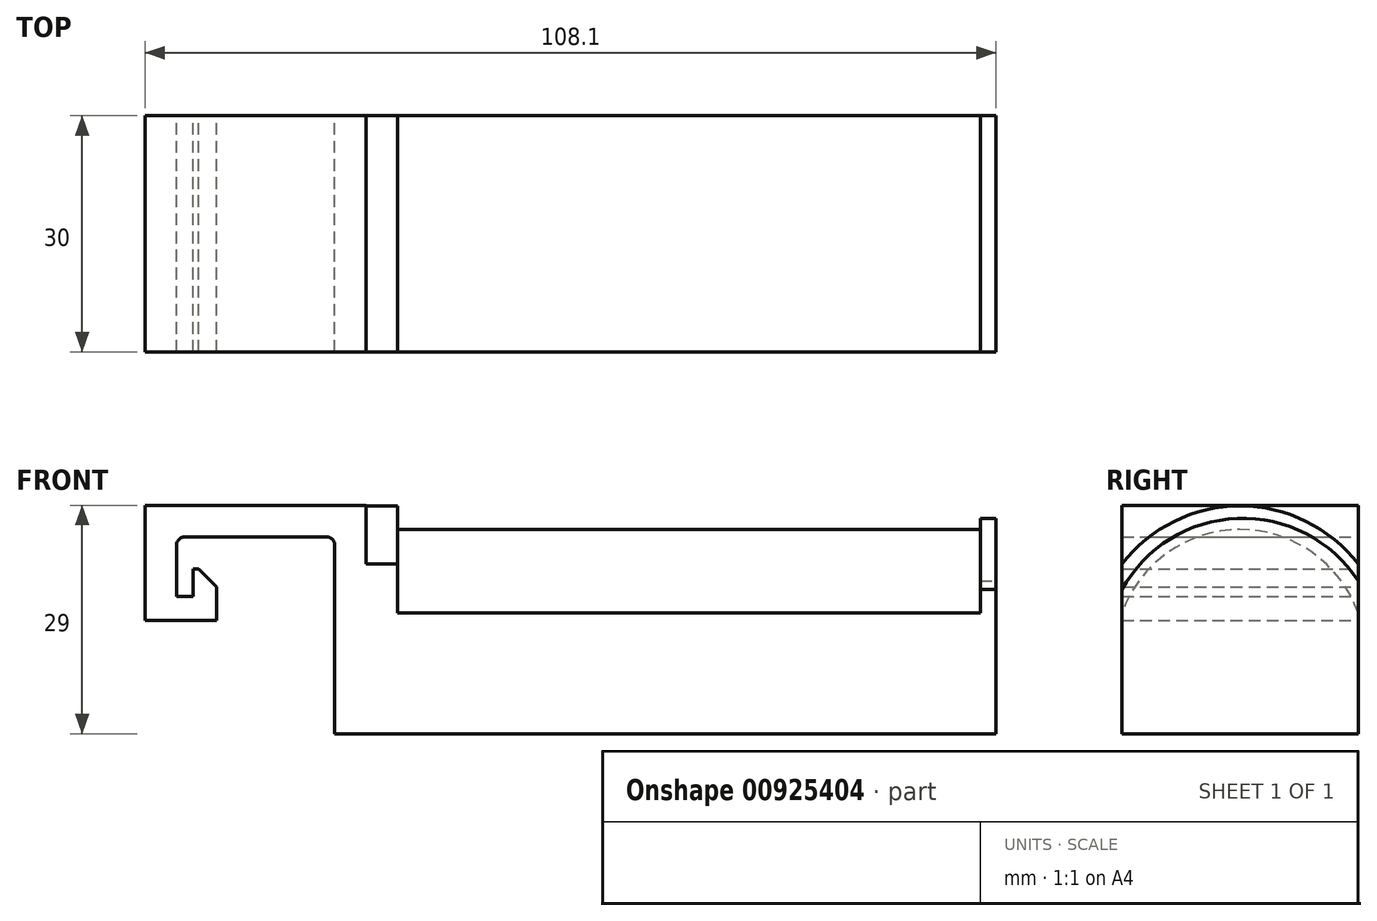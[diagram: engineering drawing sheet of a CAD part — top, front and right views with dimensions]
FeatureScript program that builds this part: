
annotation { "Feature Type Name" : "Feature", "Feature Type Description" : "" }
export const myFeature = defineFeature(function(context is Context, id is Id, definition is map)
    precondition{}
    {
        {
            var Q0;
            Q0=qCreatedBy(makeId("Front.planeOp"),FACE);
            var sketch = newSketch(context, id + "F0", { "sketchPlane" : qUnion([Q0])});
            skLineSegment(sketch, "E0", {"start": v(-34.86, 21.27) * mm, "end": v(-34.86, -2.73) * mm});
            skLineSegment(sketch, "E1", {"start": v(-22.86, 9.27) * mm, "end": v(-46.86, 9.27) * mm});
            skLineSegment(sketch, "E2", {"start": v(-25.86, 19.27) * mm, "end": v(-43.86, 19.27) * mm});
            skLineSegment(sketch, "E3", {"start": v(-25.86, -0.73) * mm, "end": v(-31.56, -0.73) * mm});
            skLineSegment(sketch, "E4", {"start": v(-24.86, 18.27) * mm, "end": v(-24.86, 0.27) * mm});
            skLineSegment(sketch, "E5", {"start": v(-44.86, 18.27) * mm, "end": v(-44.86, 12.57) * mm});
            skLineSegment(sketch, "E6", {"start": v(-30.86, 10.27) * mm, "end": v(-30.86, 6.54) * mm});
            skLineSegment(sketch, "E7", {"start": v(-38.86, 12.21) * mm, "end": v(-38.86, 9.93) * mm});
            skLineSegment(sketch, "E8", {"start": v(-33.86, 13.27) * mm, "end": v(-37.59, 13.27) * mm});
            skLineSegment(sketch, "E9", {"start": v(-27.86, 17.27) * mm, "end": v(-40.36, 17.27) * mm});
            skLineSegment(sketch, "E10", {"start": v(-26.86, 16.27) * mm, "end": v(-26.86, 3.77) * mm});
            skLineSegment(sketch, "E11", {"start": v(-42.86, 15.27) * mm, "end": v(-42.86, 12.57) * mm});
            skLineSegment(sketch, "E12", {"start": v(-43.16, 12.27) * mm, "end": v(-44.56, 12.27) * mm});
            skLineSegment(sketch, "E13", {"start": v(-43.16, 6.27) * mm, "end": v(-44.56, 6.27) * mm});
            skLineSegment(sketch, "E14", {"start": v(-41.92, 3.27) * mm, "end": v(-42.86, 3.27) * mm});
            skLineSegment(sketch, "E15", {"start": v(-42.86, 5.97) * mm, "end": v(-42.86, 3.27) * mm});
            skLineSegment(sketch, "E16", {"start": v(-44.86, 5.97) * mm, "end": v(-44.86, 0.27) * mm});
            skLineSegment(sketch, "E17", {"start": v(-41.92, 15.27) * mm, "end": v(-42.86, 15.27) * mm});
            skLineSegment(sketch, "E18", {"start": v(-38.79, 8.87) * mm, "end": v(-38.56, 9.27) * mm});
            skLineSegment(sketch, "E19", {"start": v(-38.79, 9.68) * mm, "end": v(-38.56, 9.27) * mm});
            skLineSegment(sketch, "E20", {"start": v(-38.86, 6.77) * mm, "end": v(-38.86, 6.33) * mm});
            skLineSegment(sketch, "E21", {"start": v(-38.86, 12.21) * mm, "end": v(-41.92, 15.27) * mm});
            skLineSegment(sketch, "E22", {"start": v(-38.86, 6.33) * mm, "end": v(-41.92, 3.27) * mm});
            skLineSegment(sketch, "E23", {"start": v(-38.86, 6.77) * mm, "end": v(-38.6, 8.05) * mm});
            skArc(sketch, "E24", {"start": v(-38.79, 8.87) * mm, "mid": v(-38.86, 8.62) * mm, "end": v(-38.79, 8.37) * mm});
            skLineSegment(sketch, "E25", {"start": v(-38.79, 8.37) * mm, "end": v(-38.6, 8.05) * mm});
            skArc(sketch, "E26", {"start": v(-38.86, 9.93) * mm, "mid": v(-38.84, 9.8) * mm, "end": v(-38.79, 9.68) * mm});
            skArc(sketch, "E27", {"start": v(-43.16, 12.27) * mm, "mid": v(-42.94, 12.36) * mm, "end": v(-42.86, 12.57) * mm});
            skArc(sketch, "E28", {"start": v(-44.86, 12.57) * mm, "mid": v(-44.77, 12.36) * mm, "end": v(-44.56, 12.27) * mm});
            skArc(sketch, "E29", {"start": v(-42.86, 5.97) * mm, "mid": v(-42.94, 6.19) * mm, "end": v(-43.16, 6.27) * mm});
            skArc(sketch, "E30", {"start": v(-44.56, 6.27) * mm, "mid": v(-44.77, 6.19) * mm, "end": v(-44.86, 5.97) * mm});
            skLineSegment(sketch, "E31", {"start": v(-37.8, 5.27) * mm, "end": v(-35.51, 5.27) * mm});
            skLineSegment(sketch, "E32", {"start": v(-32.36, 5.27) * mm, "end": v(-31.92, 5.27) * mm});
            skArc(sketch, "E33", {"start": v(-38.16, -0.73) * mm, "mid": v(-37.94, -0.64) * mm, "end": v(-37.86, -0.43) * mm});
            skLineSegment(sketch, "E34", {"start": v(-40.86, 1.27) * mm, "end": v(-38.16, 1.27) * mm});
            skArc(sketch, "E35", {"start": v(-37.86, 0.97) * mm, "mid": v(-37.94, 1.19) * mm, "end": v(-38.16, 1.27) * mm});
            skLineSegment(sketch, "E36", {"start": v(-31.56, 1.27) * mm, "end": v(-28.86, 1.27) * mm});
            skArc(sketch, "E37", {"start": v(-31.56, 1.27) * mm, "mid": v(-31.77, 1.19) * mm, "end": v(-31.86, 0.97) * mm});
            skLineSegment(sketch, "E38", {"start": v(-28.86, 2.21) * mm, "end": v(-28.86, 1.27) * mm});
            skLineSegment(sketch, "E39", {"start": v(-40.86, 2.21) * mm, "end": v(-40.86, 1.27) * mm});
            skLineSegment(sketch, "E40", {"start": v(-31.86, 0.97) * mm, "end": v(-31.86, -0.43) * mm});
            skArc(sketch, "E41", {"start": v(-31.86, -0.43) * mm, "mid": v(-31.77, -0.64) * mm, "end": v(-31.56, -0.73) * mm});
            skLineSegment(sketch, "E42", {"start": v(-37.86, 0.97) * mm, "end": v(-37.86, -0.43) * mm});
            skLineSegment(sketch, "E43", {"start": v(-34.45, 5.34) * mm, "end": v(-34.86, 5.57) * mm});
            skLineSegment(sketch, "E44", {"start": v(-35.26, 5.34) * mm, "end": v(-34.86, 5.57) * mm});
            skArc(sketch, "E45", {"start": v(-35.51, 5.27) * mm, "mid": v(-35.38, 5.3) * mm, "end": v(-35.26, 5.34) * mm});
            skLineSegment(sketch, "E46", {"start": v(-31.92, 5.27) * mm, "end": v(-28.86, 2.21) * mm});
            skLineSegment(sketch, "E47", {"start": v(-37.8, 5.27) * mm, "end": v(-40.86, 2.21) * mm});
            skLineSegment(sketch, "E48", {"start": v(-32.36, 5.27) * mm, "end": v(-33.64, 5.52) * mm});
            skArc(sketch, "E49", {"start": v(-34.45, 5.34) * mm, "mid": v(-34.2, 5.27) * mm, "end": v(-33.95, 5.34) * mm});
            skLineSegment(sketch, "E50", {"start": v(-33.95, 5.34) * mm, "end": v(-33.64, 5.52) * mm});
            skLineSegment(sketch, "E51", {"start": v(-38.16, -0.73) * mm, "end": v(-43.86, -0.73) * mm});
            skLineSegment(sketch, "E52", {"start": v(-30.7, 6.19) * mm, "end": v(-27.94, 3.42) * mm});
            skLineSegment(sketch, "E53", {"start": v(-37.94, 13.42) * mm, "end": v(-40.7, 16.19) * mm});
            skLineSegment(sketch, "E54", {"start": v(-40.86, 16.77) * mm, "end": v(-40.86, 16.54) * mm});
            skLineSegment(sketch, "E55", {"start": v(-27.36, 3.27) * mm, "end": v(-27.59, 3.27) * mm});
            skCircle(sketch, "E56", {"center": v(-34.86, 9.27) * mm, "radius": 2.1 * mm});
            skArc(sketch, "E57", {"start": v(-26.86, 16.27) * mm, "mid": v(-27.15, 16.98) * mm, "end": v(-27.86, 17.27) * mm});
            skArc(sketch, "E58", {"start": v(-24.86, 18.27) * mm, "mid": v(-25.15, 18.98) * mm, "end": v(-25.86, 19.27) * mm});
            skArc(sketch, "E59", {"start": v(-25.86, -0.73) * mm, "mid": v(-25.15, -0.43) * mm, "end": v(-24.86, 0.27) * mm});
            skArc(sketch, "E60", {"start": v(-44.86, 0.27) * mm, "mid": v(-44.56, -0.43) * mm, "end": v(-43.86, -0.73) * mm});
            skArc(sketch, "E61", {"start": v(-43.86, 19.27) * mm, "mid": v(-44.56, 18.98) * mm, "end": v(-44.86, 18.27) * mm});
            skArc(sketch, "E62", {"start": v(-27.36, 3.27) * mm, "mid": v(-27, 3.42) * mm, "end": v(-26.86, 3.77) * mm});
            skArc(sketch, "E63", {"start": v(-27.94, 3.42) * mm, "mid": v(-27.78, 3.31) * mm, "end": v(-27.59, 3.27) * mm});
            skArc(sketch, "E64", {"start": v(-40.36, 17.27) * mm, "mid": v(-40.7, 17.13) * mm, "end": v(-40.86, 16.77) * mm});
            skArc(sketch, "E65", {"start": v(-40.86, 16.54) * mm, "mid": v(-40.82, 16.35) * mm, "end": v(-40.7, 16.19) * mm});
            skArc(sketch, "E66", {"start": v(-37.94, 13.42) * mm, "mid": v(-37.78, 13.31) * mm, "end": v(-37.59, 13.27) * mm});
            skArc(sketch, "E67", {"start": v(-30.86, 6.54) * mm, "mid": v(-30.82, 6.35) * mm, "end": v(-30.7, 6.19) * mm});
            skArc(sketch, "E68", {"start": v(-30.86, 10.27) * mm, "mid": v(-31.74, 12.4) * mm, "end": v(-33.86, 13.27) * mm});
            skSolve(sketch);
        }
        {
            var Q0;
            Q0=makeQuery(id+"F0.imprint","IMPRINT",FACE,{"disambiguationData":[TD([[makeQuery(id+"F0.imprint","IMPRINT",EDGE,{"derivedFrom":sQuery(id+"F0.wireOp",EDGE,"E5")}),1.0]])]});
            var sketch = newSketch(context, id + "F1", { "sketchPlane" : qUnion([Q0])});
            skLineSegment(sketch, "E69.bottom", {"start": v(-42.14, 15.3) * mm, "end": v(-42.83, 15.3) * mm});
            skLineSegment(sketch, "E69.top", {"start": v(-39.83, 8.8) * mm, "end": v(-42.83, 8.8) * mm});
            skLineSegment(sketch, "E69.left", {"start": v(-39.83, 13.02) * mm, "end": v(-39.83, 8.8) * mm});
            skLineSegment(sketch, "E69.right", {"start": v(-42.83, 15.3) * mm, "end": v(-42.83, 8.8) * mm});
            skLineSegment(sketch, "E70.bottom", {"start": v(-42.83, 8.8) * mm, "end": v(-48.93, 8.8) * mm});
            skLineSegment(sketch, "E70.top", {"start": v(-42.83, 11.8) * mm, "end": v(-48.93, 11.8) * mm});
            skLineSegment(sketch, "E70.left", {"start": v(-42.83, 8.8) * mm, "end": v(-42.83, 11.8) * mm});
            skLineSegment(sketch, "E70.right", {"start": v(-48.93, 8.8) * mm, "end": v(-48.93, 11.8) * mm});
            skLineSegment(sketch, "E71.bottom", {"start": v(-48.93, 11.8) * mm, "end": v(-44.93, 11.8) * mm});
            skLineSegment(sketch, "E71.left", {"start": v(-48.93, 11.8) * mm, "end": v(-48.93, 23.39) * mm});
            skLineSegment(sketch, "E71.right", {"start": v(-44.93, 11.8) * mm, "end": v(-44.93, 18.33) * mm});
            skLineSegment(sketch, "E72.bottom", {"start": v(-48.93, 23.39) * mm, "end": v(-20.85, 23.39) * mm});
            skLineSegment(sketch, "E72.top", {"start": v(-43.87, 19.39) * mm, "end": v(-25.83, 19.39) * mm});
            skLineSegment(sketch, "E72.right", {"start": v(-20.85, 23.39) * mm, "end": v(-20.83, 19.39) * mm});
            skLineSegment(sketch, "E73.bottom", {"start": v(-20.83, 14.39) * mm, "end": v(-24.83, 14.39) * mm});
            skLineSegment(sketch, "E73.top", {"start": v(-20.83, -5.61) * mm, "end": v(-24.83, -5.61) * mm});
            skLineSegment(sketch, "E73.left", {"start": v(-20.83, 14.39) * mm, "end": v(-20.83, -5.61) * mm});
            skLineSegment(sketch, "E73.right", {"start": v(-24.83, 18.39) * mm, "end": v(-24.83, -5.61) * mm});
            skArc(sketch, "E74.filletArc", {"start": v(-43.87, 19.39) * mm, "mid": v(-44.62, 19.08) * mm, "end": v(-44.93, 18.33) * mm});
            skPoint(sketch, "E75.visualSharp", {"position": v(-39.83, 15.3) * mm});
            skPoint(sketch, "E76", {"position": v(-65.12, 18.75) * mm});
            skLineSegment(sketch, "E77", {"start": v(-42.14, 15.3) * mm, "end": v(-39.83, 13.02) * mm});
            skArc(sketch, "E78.filletArc", {"start": v(-24.83, 18.39) * mm, "mid": v(-25.12, 19.1) * mm, "end": v(-25.83, 19.39) * mm});
            skLineSegment(sketch, "E79", {"start": v(-20.83, 19.39) * mm, "end": v(-20.83, 14.39) * mm});
            skSolve(sketch);
        }
        {
            var Q0;
            Q0 = qSketchRegion(id + "F1", true);
            extrude(context, id + "F2", {"entities" : qUnion([Q0]), "endBound" : BoundingType.SYMMETRIC, "depth" : 30 * mm, "offsetDistance" : 25 * mm});
        }
        {
            var Q0;
            Q0=makeQuery(id+"F2.opExtrude","SWEPT_FACE",FACE,{"disambiguationData":[OSD([sQuery(id+"F1.wireOp",EDGE,"E73.left")])]});
            var sketch = newSketch(context, id + "F3", { "sketchPlane" : qUnion([Q0])});
            skLineSegment(sketch, "E80.bottom", {"start": v(-15, -5.61) * mm, "end": v(15, -5.61) * mm});
            skLineSegment(sketch, "E80.top", {"start": v(-15, 9.72) * mm, "end": v(15, 9.72) * mm});
            skLineSegment(sketch, "E80.left", {"start": v(-15, -5.61) * mm, "end": v(-15, 13.32) * mm});
            skLineSegment(sketch, "E80.right", {"start": v(15, -5.61) * mm, "end": v(15, 13.32) * mm});
            skArc(sketch, "E81", {"start": v(15, 9.72) * mm, "mid": v(9.18, 17.4) * mm, "end": v(0, 20.32) * mm});
            skArc(sketch, "E82", {"start": v(0, 20.32) * mm, "mid": v(-9.18, 17.4) * mm, "end": v(-15, 9.72) * mm});
            skArc(sketch, "E83.0", {"start": v(0, 23.32) * mm, "mid": v(-8.36, 21.38) * mm, "end": v(-15, 15.93) * mm});
            skArc(sketch, "E83.1", {"start": v(15, 15.93) * mm, "mid": v(8.36, 21.38) * mm, "end": v(0, 23.32) * mm});
            skLineSegment(sketch, "E84", {"start": v(-15, 9.72) * mm, "end": v(-15, 15.93) * mm});
            skLineSegment(sketch, "E85", {"start": v(15, 9.72) * mm, "end": v(15, 15.93) * mm});
            skSolve(sketch);
        }
        {
            var Q0;
            Q0=makeQuery(id+"F3.imprint","IMPRINT",FACE,{"disambiguationData":[TD([[makeQuery(id+"F3.imprint","IMPRINT",EDGE,{"derivedFrom":sQuery(id+"F3.wireOp",EDGE,"E80.top")}),1.0]])]});
            var Q1;
            Q1=makeQuery(id+"F3.imprint","IMPRINT",FACE,{"disambiguationData":[TD([[makeQuery(id+"F3.imprint","IMPRINT",EDGE,{"derivedFrom":sQuery(id+"F3.wireOp",EDGE,"E80.bottom")}),1.0]])]});
            var Q2;
            {var subQ0=sQuery(id+"F3.wireOp",EDGE,"E82");var subQ1=sQuery(id+"F3.wireOp",EDGE,"E81");var subQ2=makeQuery(id+"F3.imprint","INTERSECT",VERTEX,{"derivedFrom":[subQ1,subQ0]});Q2=makeQuery(id+"F3.imprint","IMPRINT",FACE,{"disambiguationData":[TD([[makeQuery(id+"F3.imprint","IMPRINT",EDGE,{"disambiguationData":[TD([[subQ2,1.0]])],"derivedFrom":subQ1}),1.0]])]});}
            extrude(context, id + "F4", {"entities" : qUnion([Q0, Q1, Q2]), "depth" : 80 * mm, "offsetDistance" : 25 * mm});
        }
        {
            var Q0;
            Q0 = qSketchRegion(id + "F3", true);
            extrude(context, id + "F5", {"entities" : qUnion([Q0]), "operationType" : NewBodyOperationType.ADD, "depth" : 4 * mm, "offsetDistance" : 25 * mm});
        }
        {
            var Q0;
            Q0=makeQuery(id+"F4.opExtrude","CAP_FACE",FACE,{"disambiguationData":[OSD([sQuery(id+"F3.wireOp",EDGE,"E80.bottom"),sQuery(id+"F3.wireOp",EDGE,"E80.left"),sQuery(id+"F3.wireOp",EDGE,"E80.right"),sQuery(id+"F3.wireOp",EDGE,"E81"),sQuery(id+"F3.wireOp",EDGE,"E82")])],"isStart":false});
            var sketch = newSketch(context, id + "F6", { "sketchPlane" : qUnion([Q0])});
            skArc(sketch, "E86.0", {"start": v(15, 13.83) * mm, "mid": v(-0.32, 21.74) * mm, "end": v(-15, 12.7) * mm});
            skLineSegment(sketch, "E87", {"start": v(-15, 9.72) * mm, "end": v(-15, 12.7) * mm});
            skLineSegment(sketch, "E88", {"start": v(15, 9.72) * mm, "end": v(15, 13.83) * mm});
            skLineSegment(sketch, "E89", {"start": v(15, -5.61) * mm, "end": v(-15, -5.61) * mm});
            skPoint(sketch, "E86.1.end.orphan", {"position": v(14.53, 14.52) * mm});
            skPoint(sketch, "E86.1.start.orphan", {"position": v(14.53, 13.85) * mm});
            skSolve(sketch);
        }
        {
            var Q0;
            Q0=makeQuery(id+"F6.imprint","IMPRINT",FACE,{"disambiguationData":[TD([[makeQuery(id+"F6.imprint","IMPRINT",EDGE,{"derivedFrom":sQuery(id+"F6.wireOp",EDGE,"E86.0")}),1.0]])]});
            extrude(context, id + "F7", {"entities" : qUnion([Q0]), "operationType" : NewBodyOperationType.ADD, "oppositeDirection" : true, "depth" : 2 * mm, "offsetDistance" : 25 * mm});
        }
    });
